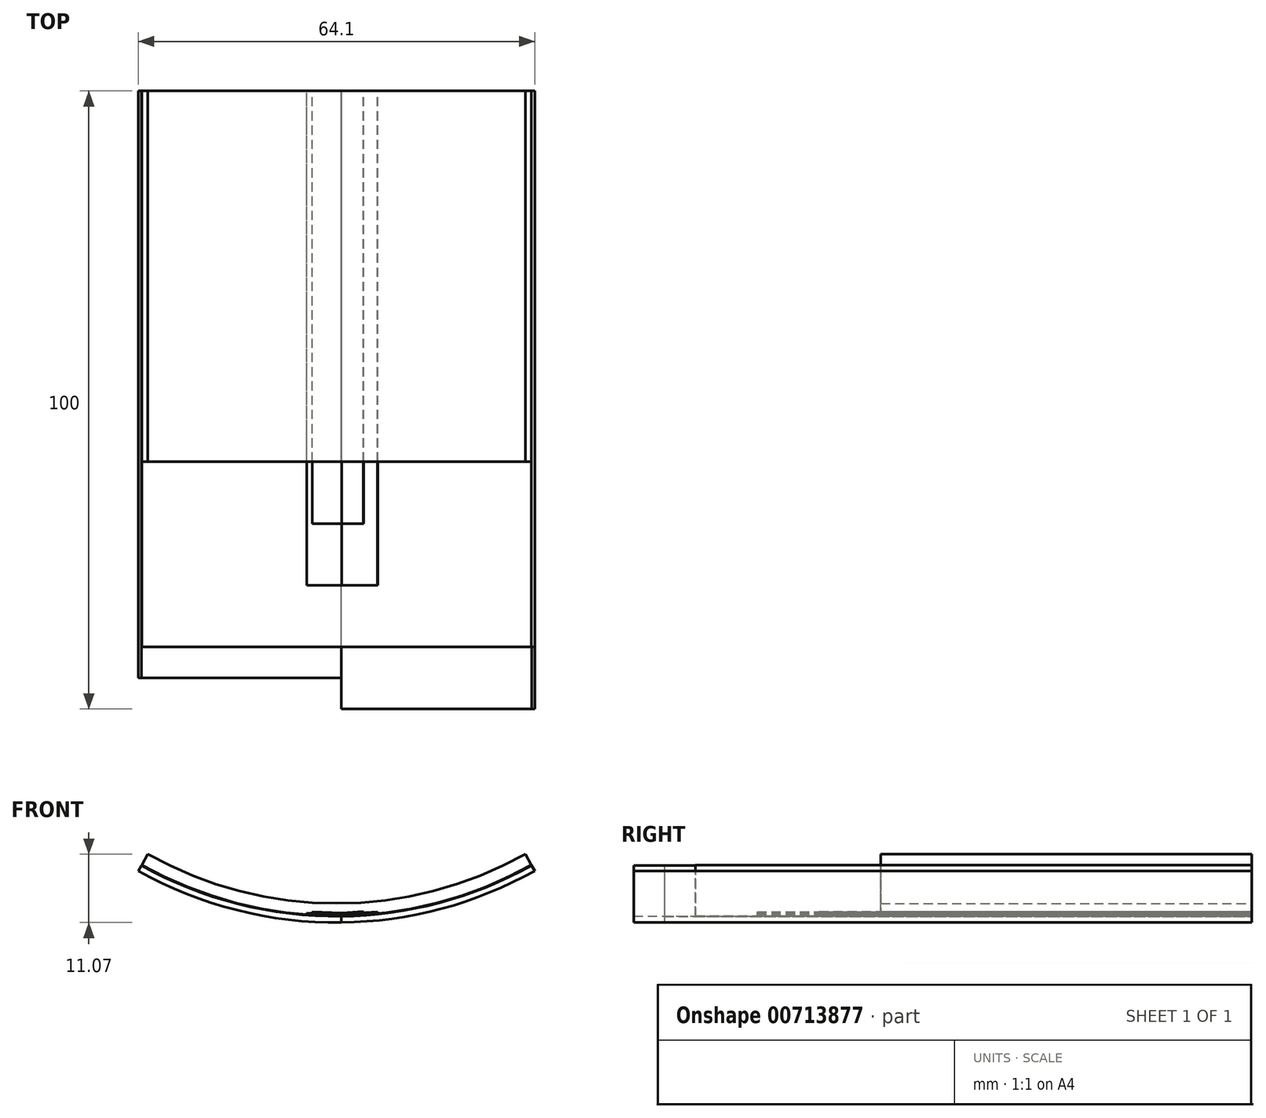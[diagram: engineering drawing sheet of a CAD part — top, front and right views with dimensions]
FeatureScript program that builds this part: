
annotation { "Feature Type Name" : "Feature", "Feature Type Description" : "" }
export const myFeature = defineFeature(function(context is Context, id is Id, definition is map)
    precondition{}
    {
        {
            var Q0;
            Q0=qCreatedBy(makeId("Front.planeOp"),FACE);
            var sketch = newSketch(context, id + "F0", { "sketchPlane" : qUnion([Q0])});
            skArc(sketch, "E0", {"start": v(-33.6, 14.22) * mm, "mid": v(-2.04, 6) * mm, "end": v(29.52, 14.23) * mm});
            skArc(sketch, "E1.1", {"start": v(-34.09, 13.35) * mm, "mid": v(-2.04, 5) * mm, "end": v(30.01, 13.35) * mm});
            skArc(sketch, "E2.0", {"start": v(-33.55, 14.3) * mm, "mid": v(-2.08, 6.1) * mm, "end": v(29.4, 14.28) * mm});
            skArc(sketch, "E3.0", {"start": v(-32.57, 16.05) * mm, "mid": v(-2.04, 8.1) * mm, "end": v(28.5, 16.06) * mm});
            skLineSegment(sketch, "E4", {"start": v(-32.57, 16.05) * mm, "end": v(-34.09, 13.35) * mm});
            skLineSegment(sketch, "E5", {"start": v(28.5, 16.06) * mm, "end": v(30.01, 13.35) * mm});
            skLineSegment(sketch, "E6", {"start": v(29.4, 14.28) * mm, "end": v(29.47, 14.31) * mm});
            skLineSegment(sketch, "E7", {"start": v(-1.22, 6.32) * mm, "end": v(4.6, 6.72) * mm});
            skLineSegment(sketch, "E8", {"start": v(4.6, 6.72) * mm, "end": v(4.62, 6.44) * mm});
            skLineSegment(sketch, "E9", {"start": v(-1.22, 6.32) * mm, "end": v(-6.86, 6.55) * mm});
            skLineSegment(sketch, "E10", {"start": v(-6.86, 6.55) * mm, "end": v(-6.86, 6.27) * mm});
            skLineSegment(sketch, "E11", {"start": v(-5.99, 6.52) * mm, "end": v(-5.98, 6.72) * mm});
            skLineSegment(sketch, "E12", {"start": v(-5.98, 6.72) * mm, "end": v(-1.22, 6.55) * mm});
            skLineSegment(sketch, "E13", {"start": v(-1.22, 6.55) * mm, "end": v(2.3, 6.8) * mm});
            skLineSegment(sketch, "E14", {"start": v(2.3, 6.8) * mm, "end": v(2.32, 6.55) * mm});
            skLineSegment(sketch, "E15", {"start": v(-1.24, 6) * mm, "end": v(-1.24, 5) * mm});
            skLineSegment(sketch, "E16", {"start": v(29.52, 14.23) * mm, "end": v(30.01, 13.35) * mm});
            skSolve(sketch);
        }
        {
            var Q0;
            {var subQ2=sQuery(id+"F0.wireOp",EDGE,"E15");Q0=makeQuery(id+"F0.imprint","IMPRINT",FACE,{"disambiguationData":[TD([[makeQuery(id+"F0.imprint","IMPRINT",EDGE,{"derivedFrom":subQ2}),1.0]])]});}
            extrude(context, id + "F1", {"entities" : qUnion([Q0]), "depth" : 100 * mm});
        }
        {
            var Q0;
            {var subQ0=sQuery(id+"F0.wireOp",EDGE,"E15");Q0=makeQuery(id+"F0.imprint","IMPRINT",FACE,{"disambiguationData":[TD([[makeQuery(id+"F0.imprint","IMPRINT",EDGE,{"derivedFrom":subQ0}),-1.0]])]});}
            extrude(context, id + "F2", {"entities" : qUnion([Q0]), "depth" : 95 * mm});
        }
        {
            var Q0;
            {var subQ8=sQuery(id+"F0.wireOp",EDGE,"E6");Q0=makeQuery(id+"F0.imprint","IMPRINT",FACE,{"disambiguationData":[TD([[makeQuery(id+"F0.imprint","IMPRINT",EDGE,{"derivedFrom":subQ8}),-1.0]])]});}
            extrude(context, id + "F3", {"entities" : qUnion([Q0]), "depth" : 90 * mm});
        }
        {
            var Q0;
            {var subQ0=sQuery(id+"F0.wireOp",EDGE,"E8");Q0=makeQuery(id+"F0.imprint","IMPRINT",FACE,{"disambiguationData":[TD([[makeQuery(id+"F0.imprint","IMPRINT",EDGE,{"derivedFrom":subQ0}),-1.0]])]});}
            extrude(context, id + "F4", {"entities" : qUnion([Q0]), "depth" : 80 * mm});
        }
        {
            var Q0;
            {var subQ0=sQuery(id+"F0.wireOp",EDGE,"E11");Q0=makeQuery(id+"F0.imprint","IMPRINT",FACE,{"disambiguationData":[TD([[makeQuery(id+"F0.imprint","IMPRINT",EDGE,{"derivedFrom":subQ0}),-1.0]])]});}
            extrude(context, id + "F5", {"entities" : qUnion([Q0]), "depth" : 70 * mm});
        }
        {
            var Q0;
            {var subQ3=sQuery(id+"F0.wireOp",EDGE,"E3.0");Q0=makeQuery(id+"F0.imprint","IMPRINT",FACE,{"disambiguationData":[TD([[makeQuery(id+"F0.imprint","IMPRINT",EDGE,{"derivedFrom":subQ3}),-1.0]])]});}
            extrude(context, id + "F6", {"entities" : qUnion([Q0]), "depth" : 60 * mm});
        }
    });
